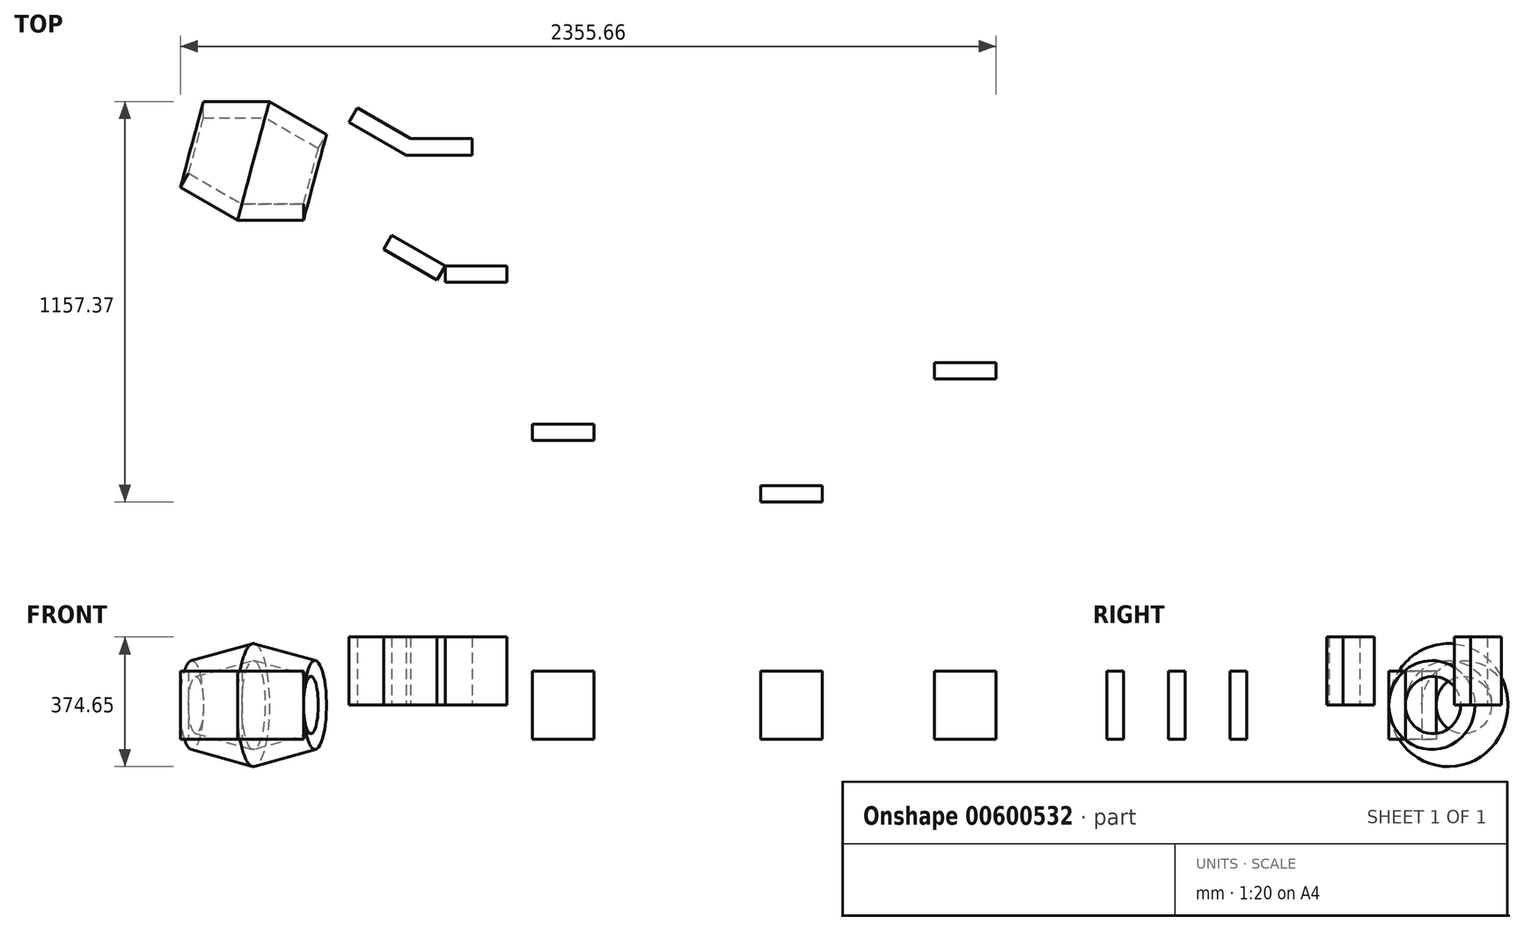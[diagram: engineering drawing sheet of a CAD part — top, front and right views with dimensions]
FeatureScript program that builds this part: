
annotation { "Feature Type Name" : "Feature", "Feature Type Description" : "" }
export const myFeature = defineFeature(function(context is Context, id is Id, definition is map)
    precondition{}
    {
        {
            var Q0;
            Q0=qCreatedBy(makeId("Top.planeOp"),FACE);
            var sketch = newSketch(context, id + "F0", { "sketchPlane" : qUnion([Q0])});
            skLineSegment(sketch, "E0.bottom", {"start": v(-281.63, -173.28) * mm, "end": v(-91.13, -173.28) * mm});
            skLineSegment(sketch, "E0.top", {"start": v(-268.93, -125.89) * mm, "end": v(-91.13, -125.89) * mm});
            skLineSegment(sketch, "E0.right", {"start": v(-91.13, -173.28) * mm, "end": v(-91.13, -125.89) * mm});
            skLineSegment(sketch, "E1", {"start": v(-268.93, -125.89) * mm, "end": v(-281.63, -173.28) * mm});
            skLineSegment(sketch, "E2", {"start": v(-281.63, -173.28) * mm, "end": v(-446.6, -78.03) * mm});
            skLineSegment(sketch, "E3", {"start": v(-446.6, -78.03) * mm, "end": v(-422.9, -36.99) * mm});
            skLineSegment(sketch, "E4", {"start": v(-422.9, -36.99) * mm, "end": v(-268.93, -125.89) * mm});
            skLineSegment(sketch, "E5.bottom", {"start": v(205.48, 15.66) * mm, "end": v(395.98, 15.66) * mm});
            skLineSegment(sketch, "E5.top", {"start": v(218.18, 63.05) * mm, "end": v(395.98, 63.05) * mm});
            skLineSegment(sketch, "E5.right", {"start": v(395.98, 15.66) * mm, "end": v(395.98, 63.05) * mm});
            skLineSegment(sketch, "E6", {"start": v(218.18, 63.05) * mm, "end": v(205.48, 15.66) * mm});
            skLineSegment(sketch, "E7", {"start": v(205.48, 15.66) * mm, "end": v(40.5, 110.9) * mm});
            skLineSegment(sketch, "E8", {"start": v(40.5, 110.9) * mm, "end": v(64.2, 151.95) * mm});
            skLineSegment(sketch, "E9", {"start": v(64.2, 151.95) * mm, "end": v(218.18, 63.05) * mm});
            skLineSegment(sketch, "E10", {"start": v(-281.63, -173.28) * mm, "end": v(-235.6, -1.54) * mm, "construction": true});
            skLineSegment(sketch, "E11", {"start": v(-379.07, 36.9) * mm, "end": v(0, -64.67) * mm, "construction": true});
            skLineSegment(sketch, "E12.bottom", {"start": v(495.86, -352.5) * mm, "end": v(318.06, -352.5) * mm});
            skLineSegment(sketch, "E12.top", {"start": v(495.86, -305.11) * mm, "end": v(318.06, -305.11) * mm});
            skLineSegment(sketch, "E12.left", {"start": v(495.86, -352.5) * mm, "end": v(495.86, -305.11) * mm});
            skLineSegment(sketch, "E12.right", {"start": v(318.06, -352.5) * mm, "end": v(318.06, -305.11) * mm});
            skLineSegment(sketch, "E13", {"start": v(318.06, -305.11) * mm, "end": v(164.08, -216.21) * mm});
            skLineSegment(sketch, "E14", {"start": v(164.08, -216.21) * mm, "end": v(140.38, -257.26) * mm});
            skLineSegment(sketch, "E15", {"start": v(140.38, -257.26) * mm, "end": v(294.36, -346.16) * mm});
            skLineSegment(sketch, "E16", {"start": v(294.36, -346.16) * mm, "end": v(318.06, -305.11) * mm});
            skSolve(sketch);
        }
        {
            var Q0;
            Q0=makeQuery(id+"F0.imprint","IMPRINT",FACE,{"disambiguationData":[TD([[makeQuery(id+"F0.imprint","IMPRINT",EDGE,{"derivedFrom":sQuery(id+"F0.wireOp",EDGE,"E5.bottom")}),1.0]])]});
            var Q1;
            Q1=makeQuery(id+"F0.imprint","IMPRINT",FACE,{"disambiguationData":[TD([[makeQuery(id+"F0.imprint","IMPRINT",EDGE,{"derivedFrom":sQuery(id+"F0.wireOp",EDGE,"E6")}),-1.0]])]});
            extrude(context, id + "F1", {"entities" : qUnion([Q0, Q1]), "depth" : 196.85 * mm, "offsetDistance" : 25.4 * mm});
        }
        {
            var Q0;
            Q0=makeQuery(id+"F0.imprint","IMPRINT",FACE,{"disambiguationData":[TD([[makeQuery(id+"F0.imprint","IMPRINT",EDGE,{"derivedFrom":sQuery(id+"F0.wireOp",EDGE,"E1")}),-1.0]])]});
            var Q1;
            Q1=makeQuery(id+"F0.imprint","IMPRINT",FACE,{"disambiguationData":[TD([[makeQuery(id+"F0.imprint","IMPRINT",EDGE,{"derivedFrom":sQuery(id+"F0.wireOp",EDGE,"E0.bottom")}),1.0]])]});
            var Q2;
            Q2=sQuery(id+"F0.wireOp",EDGE,"E11");
            revolve(context, id + "F2", {"entities" : qUnion([Q0, Q1]), "axis" : qUnion([Q2]), "revolveType" : RevolveType.FULL});
        }
        {
            var Q0;
            Q0=makeQuery(id+"F0.imprint","IMPRINT",FACE,{"disambiguationData":[TD([[makeQuery(id+"F0.imprint","IMPRINT",EDGE,{"derivedFrom":sQuery(id+"F0.wireOp",EDGE,"E13")}),1.0]])]});
            var Q1;
            Q1=makeQuery(id+"F0.imprint","IMPRINT",FACE,{"disambiguationData":[TD([[makeQuery(id+"F0.imprint","IMPRINT",EDGE,{"derivedFrom":sQuery(id+"F0.wireOp",EDGE,"E12.bottom")}),-1.0]])]});
            extrude(context, id + "F3", {"entities" : qUnion([Q0, Q1]), "depth" : 196.85 * mm, "offsetDistance" : 25.4 * mm});
        }
        {
            var Q0;
            Q0=qCreatedBy(makeId("Top.planeOp"),FACE);
            var sketch = newSketch(context, id + "F4", { "sketchPlane" : qUnion([Q0])});
            skLineSegment(sketch, "E17.bottom", {"start": v(1228.7, -987.17) * mm, "end": v(1406.5, -987.17) * mm});
            skLineSegment(sketch, "E17.top", {"start": v(1228.7, -939.77) * mm, "end": v(1406.5, -939.77) * mm});
            skLineSegment(sketch, "E17.left", {"start": v(1228.7, -987.17) * mm, "end": v(1228.7, -939.77) * mm});
            skLineSegment(sketch, "E17.right", {"start": v(1406.5, -987.17) * mm, "end": v(1406.5, -939.77) * mm});
            skLineSegment(sketch, "E18.bottom", {"start": v(569.44, -809.37) * mm, "end": v(747.24, -809.37) * mm});
            skLineSegment(sketch, "E18.top", {"start": v(569.44, -761.97) * mm, "end": v(747.24, -761.97) * mm});
            skLineSegment(sketch, "E18.left", {"start": v(569.44, -809.37) * mm, "end": v(569.44, -761.97) * mm});
            skLineSegment(sketch, "E18.right", {"start": v(747.24, -809.37) * mm, "end": v(747.24, -761.97) * mm});
            skLineSegment(sketch, "E19.bottom", {"start": v(1731.26, -631.57) * mm, "end": v(1909.06, -631.57) * mm});
            skLineSegment(sketch, "E19.top", {"start": v(1731.26, -584.17) * mm, "end": v(1909.06, -584.17) * mm});
            skLineSegment(sketch, "E19.left", {"start": v(1731.26, -631.57) * mm, "end": v(1731.26, -584.17) * mm});
            skLineSegment(sketch, "E19.right", {"start": v(1909.06, -631.57) * mm, "end": v(1909.06, -584.17) * mm});
            skSolve(sketch);
        }
        {
            var Q0;
            Q0 = qSketchRegion(id + "F4", true);
            extrude(context, id + "F5", {"entities" : qUnion([Q0]), "endBound" : BoundingType.SYMMETRIC, "depth" : 196.85 * mm, "offsetDistance" : 25.4 * mm});
        }
        {
            var Q0;
            Q0=makeQuery(id+"F0.imprint","IMPRINT",FACE,{"disambiguationData":[TD([[makeQuery(id+"F0.imprint","IMPRINT",EDGE,{"derivedFrom":sQuery(id+"F0.wireOp",EDGE,"E0.bottom")}),1.0]])]});
            var Q1;
            Q1=makeQuery(id+"F0.imprint","IMPRINT",FACE,{"disambiguationData":[TD([[makeQuery(id+"F0.imprint","IMPRINT",EDGE,{"derivedFrom":sQuery(id+"F0.wireOp",EDGE,"E1")}),-1.0]])]});
            extrude(context, id + "F6", {"entities" : qUnion([Q0, Q1]), "endBound" : BoundingType.SYMMETRIC, "depth" : 196.85 * mm, "offsetDistance" : 25.4 * mm});
        }
    });
